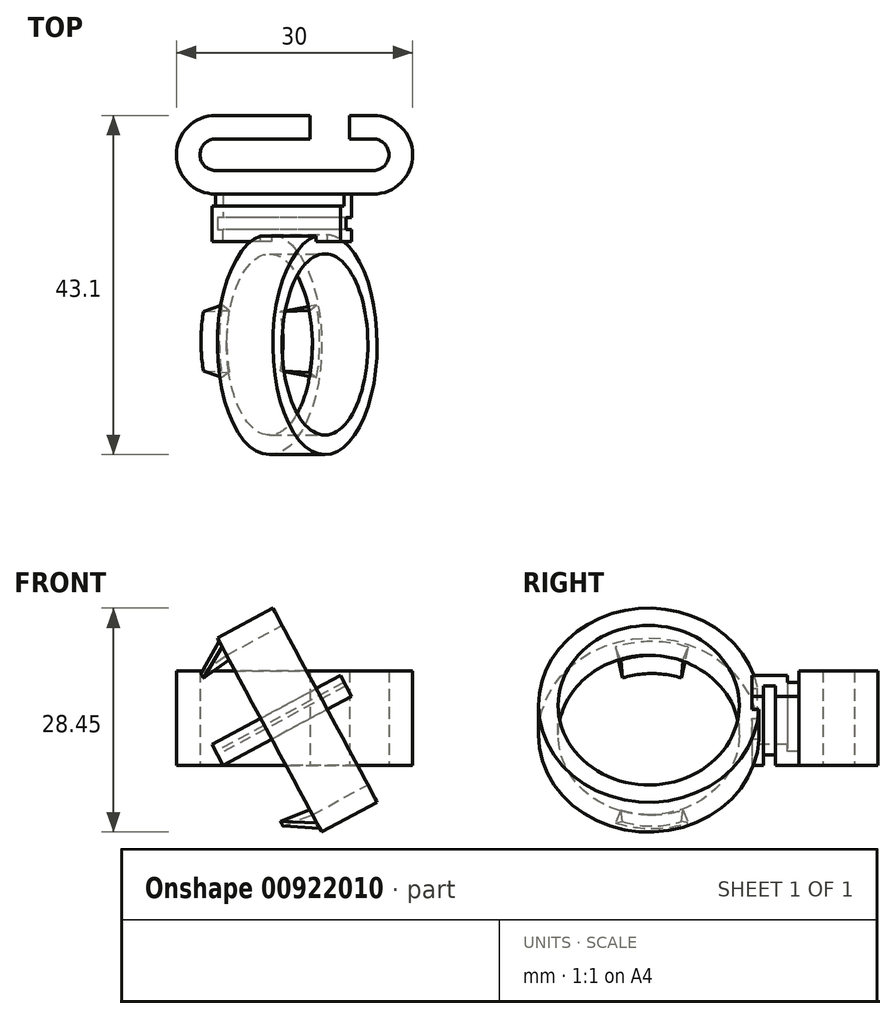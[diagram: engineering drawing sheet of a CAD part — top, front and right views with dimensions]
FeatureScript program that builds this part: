
annotation { "Feature Type Name" : "Feature", "Feature Type Description" : "" }
export const myFeature = defineFeature(function(context is Context, id is Id, definition is map)
    precondition{}
    {
        {
            var Q0;
            Q0=qCreatedBy(makeId("Top.planeOp"),FACE);
            var sketch = newSketch(context, id + "F0", { "sketchPlane" : qUnion([Q0])});
            skLineSegment(sketch, "E0", {"start": v(-20, 0) * mm, "end": v(0, 0) * mm});
            skArc(sketch, "E1", {"start": v(-20, 0) * mm, "mid": v(-22, 2) * mm, "end": v(-20, 4) * mm});
            skArc(sketch, "E2", {"start": v(0, 0) * mm, "mid": v(2, 2) * mm, "end": v(0, 4) * mm});
            skLineSegment(sketch, "E3", {"start": v(0, 4) * mm, "end": v(-3, 4) * mm});
            skLineSegment(sketch, "E4", {"start": v(-20, 4) * mm, "end": v(-8, 4) * mm});
            skLineSegment(sketch, "E5", {"start": v(-8, 4) * mm, "end": v(-8, 7) * mm});
            skLineSegment(sketch, "E6", {"start": v(-8, 7) * mm, "end": v(-20, 7) * mm});
            skLineSegment(sketch, "E7", {"start": v(-3, 4) * mm, "end": v(-3, 7) * mm});
            skLineSegment(sketch, "E8", {"start": v(-3, 7) * mm, "end": v(0, 7) * mm});
            skLineSegment(sketch, "E9", {"start": v(0, -3) * mm, "end": v(-20, -3) * mm});
            skArc(sketch, "E10", {"start": v(-20, -3) * mm, "mid": v(-25, 2) * mm, "end": v(-20, 7) * mm});
            skArc(sketch, "E11", {"start": v(0, -3) * mm, "mid": v(5, 2) * mm, "end": v(0, 7) * mm});
            skSolve(sketch);
        }
        {
            var Q0;
            Q0=makeQuery(id+"F0.imprint","IMPRINT",FACE,{"disambiguationData":[TD([[makeQuery(id+"F0.imprint","IMPRINT",EDGE,{"derivedFrom":sQuery(id+"F0.wireOp",EDGE,"E0")}),-1.0]])]});
            extrude(context, id + "F1", {"entities" : qUnion([Q0]), "depth" : 12 * mm, "offsetDistance" : 25 * mm});
        }
        {
            var Q0;
            Q0=makeQuery(id+"F1.opExtrude","SWEPT_FACE",FACE,{"disambiguationData":[OSD([sQuery(id+"F0.wireOp",EDGE,"E9")])]});
            var sketch = newSketch(context, id + "F2", { "sketchPlane" : qUnion([Q0])});
            skLineSegment(sketch, "E12", {"start": v(-20, 1.76) * mm, "end": v(-19.05, 0) * mm});
            skLineSegment(sketch, "E13", {"start": v(-19.05, 0) * mm, "end": v(0, 10.24) * mm});
            skLineSegment(sketch, "E14", {"start": v(0, 10.24) * mm, "end": v(-0.95, 12) * mm});
            skLineSegment(sketch, "E15", {"start": v(-0.95, 12) * mm, "end": v(-20, 1.76) * mm});
            skSolve(sketch);
        }
        {
            var Q0;
            Q0=sQuery(id+"F2.wireOp",EDGE,"E12");
            cPlane(context, id + "F3", {"entities" : qUnion([Q0]), "cplaneType" : CPlaneType.LINE_ANGLE, "offset" : 25 * mm, "angle" : 0 * degree, "oppositeDirection" : true, "width" : 150 * mm, "height" : 150 * mm});
        }
        {
            var Q0;
            Q0=qCreatedBy(id+"F3.planeOp",FACE);
            var sketch = newSketch(context, id + "F4", { "sketchPlane" : qUnion([Q0])});
            skLineSegment(sketch, "E16", {"start": v(3, 9.02) * mm, "end": v(6, 9.02) * mm});
            skLineSegment(sketch, "E17", {"start": v(3, 11.02) * mm, "end": v(4.5, 11.02) * mm});
            skLineSegment(sketch, "E18", {"start": v(4.5, 11.02) * mm, "end": v(4.5, 12.02) * mm});
            skLineSegment(sketch, "E19", {"start": v(4.5, 12.02) * mm, "end": v(9, 12.02) * mm});
            skLineSegment(sketch, "E20", {"start": v(9, 12.02) * mm, "end": v(9, 9.02) * mm});
            skLineSegment(sketch, "E21", {"start": v(9, 9.02) * mm, "end": v(7.5, 9.02) * mm});
            skLineSegment(sketch, "E22", {"start": v(6, 9.02) * mm, "end": v(6, 10.52) * mm});
            skLineSegment(sketch, "E23", {"start": v(6, 10.52) * mm, "end": v(7.5, 10.52) * mm});
            skLineSegment(sketch, "E24", {"start": v(7.5, 10.52) * mm, "end": v(7.5, 9.02) * mm});
            skLineSegment(sketch, "E25", {"start": v(3, 9.02) * mm, "end": v(3, 11.02) * mm});
            skSolve(sketch);
        }
        {
            var Q0;
            Q0 = qSketchRegion(id + "F4", true);
            extrude(context, id + "F5", {"entities" : qUnion([Q0]), "operationType" : NewBodyOperationType.ADD, "oppositeDirection" : true, "depth" : 18.5 * mm, "offsetDistance" : 25 * mm});
        }
        {
            var Q0;
            Q0=qCreatedBy(id+"F3.planeOp",FACE);
            cPlane(context, id + "F6", {"entities" : qUnion([Q0]), "cplaneType" : CPlaneType.OFFSET, "offset" : 15 * mm, "oppositeDirection" : true, "width" : 150 * mm, "height" : 150 * mm});
        }
        {
            var Q0;
            Q0=qCreatedBy(id+"F6.planeOp",FACE);
            var sketch = newSketch(context, id + "F7", { "sketchPlane" : qUnion([Q0])});
            skLineSegment(sketch, "E26", {"start": v(9, 19.71) * mm, "end": v(9, -1.69) * mm});
            skCircle(sketch, "E27", {"center": v(22.1, 9.62) * mm, "radius": 11.5 * mm});
            skCircle(sketch, "E28", {"center": v(22.1, 9.62) * mm, "radius": 14 * mm});
            skSolve(sketch);
        }
        {
            var Q0;
            Q0=makeQuery(id+"F7.imprint","IMPRINT",FACE,{"disambiguationData":[TD([[makeQuery(id+"F7.imprint","IMPRINT",EDGE,{"derivedFrom":sQuery(id+"F7.wireOp",EDGE,"E27")}),-1.0]])]});
            var Q1;
            {var subQ0=sQuery(id+"F7.wireOp",EDGE,"E28");var subQ1=sQuery(id+"F7.wireOp",EDGE,"E26");var subQ2=makeQuery(id+"F7.imprint","INTERSECT",VERTEX,{"disambiguationData":[OD(0.0)],"derivedFrom":[subQ1,subQ0]});Q1=makeQuery(id+"F7.imprint","IMPRINT",FACE,{"disambiguationData":[TD([[makeQuery(id+"F7.imprint","IMPRINT",EDGE,{"disambiguationData":[TD([[subQ2,-1.0]])],"derivedFrom":subQ1}),-1.0]])]});}
            extrude(context, id + "F8", {"entities" : qUnion([Q0, Q1]), "operationType" : NewBodyOperationType.ADD, "depth" : 8 * mm, "offsetDistance" : 25 * mm});
        }
        {
            var Q0;
            Q0=qCreatedBy(makeId("Front.planeOp"),FACE);
            cPlane(context, id + "F9", {"entities" : qUnion([Q0]), "cplaneType" : CPlaneType.OFFSET, "offset" : 21.7 * mm, "width" : 150 * mm, "height" : 150 * mm});
        }
        {
            var Q0;
            Q0=qCreatedBy(id+"F9.planeOp",FACE);
            var sketch = newSketch(context, id + "F10", { "sketchPlane" : qUnion([Q0])});
            skLineSegment(sketch, "E29.0", {"start": v(-7.73, -6.28) * mm, "end": v(-18.62, 13.98) * mm});
            skPoint(sketch, "E30", {"position": v(-13.17, 3.85) * mm});
            skLineSegment(sketch, "E31", {"start": v(-13.17, 3.85) * mm, "end": v(-17.55, 1.5) * mm});
            skLineSegment(sketch, "E32", {"start": v(-7.73, -6.28) * mm, "end": v(-6.8, -8.03) * mm});
            skLineSegment(sketch, "E33", {"start": v(-6.8, -8.03) * mm, "end": v(-11.46, -7.72) * mm});
            skLineSegment(sketch, "E34", {"start": v(-11.46, -7.72) * mm, "end": v(-7.73, -6.28) * mm});
            skLineSegment(sketch, "E35.MirrorCS", {"start": v(-21.88, 11.66) * mm, "end": v(-18.62, 13.98) * mm});
            skLineSegment(sketch, "E36.MirrorCS", {"start": v(-19.55, 15.72) * mm, "end": v(-21.88, 11.66) * mm});
            skLineSegment(sketch, "E37.MirrorCS", {"start": v(-18.62, 13.98) * mm, "end": v(-19.55, 15.72) * mm});
            skSolve(sketch);
        }
        {
            var Q0;
            Q0=makeQuery(id+"F10.imprint","IMPRINT",FACE,{"disambiguationData":[TD([[makeQuery(id+"F10.imprint","IMPRINT",EDGE,{"derivedFrom":sQuery(id+"F10.wireOp",EDGE,"E32")}),-1.0]])]});
            var Q1;
            Q1=makeQuery(id+"F10.imprint","IMPRINT",FACE,{"disambiguationData":[TD([[makeQuery(id+"F10.imprint","IMPRINT",EDGE,{"derivedFrom":sQuery(id+"F10.wireOp",EDGE,"E35.MirrorCS")}),1.0]])]});
            var Q2;
            Q2=sQuery(id+"F10.wireOp",EDGE,"E31");
            revolve(context, id + "F11", {"operationType" : NewBodyOperationType.ADD, "surfaceOperationType" : NewSurfaceOperationType.NEW, "entities" : qUnion([Q0, Q1]), "axis" : qUnion([Q2]), "revolveType" : RevolveType.SYMMETRIC, "angle" : 40 * degree});
        }
    });
